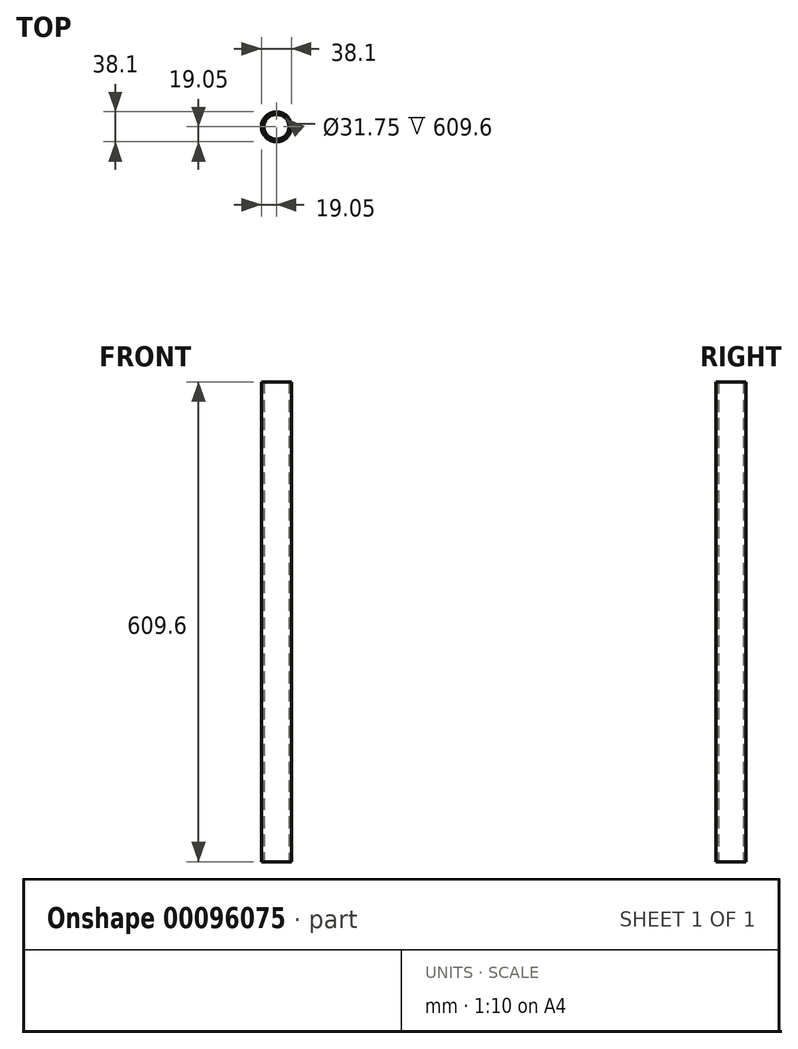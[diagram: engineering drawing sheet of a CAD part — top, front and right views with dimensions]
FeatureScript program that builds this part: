
annotation { "Feature Type Name" : "Feature", "Feature Type Description" : "" }
export const myFeature = defineFeature(function(context is Context, id is Id, definition is map)
    precondition{}
    {
        {
            var Q0;
            Q0=qCreatedBy(makeId("Top.planeOp"),FACE);
            var sketch = newSketch(context, id + "F0", { "sketchPlane" : qUnion([Q0])});
            skCircle(sketch, "E0", {"center": v(0, 0) * mm, "radius": 19.05 * mm});
            skCircle(sketch, "E1", {"center": v(0, 0) * mm, "radius": 15.88 * mm});
            skSolve(sketch);
        }
        {
            var Q0;
            Q0=makeQuery(id+"F0.imprint","IMPRINT",FACE,{"disambiguationData":[TD([[makeQuery(id+"F0.imprint","IMPRINT",EDGE,{"derivedFrom":sQuery(id+"F0.wireOp",EDGE,"E0")}),1.0]])]});
            extrude(context, id + "F1", {"entities" : qUnion([Q0]), "depth" : 609.6 * mm});
        }
        {
            var Q0;
            Q0=qCreatedBy(makeId("Top.planeOp"),FACE);
            cPlane(context, id + "F2", {"entities" : qUnion([Q0]), "cplaneType" : CPlaneType.OFFSET, "offset" : 609.6 * mm, "width" : 152.4 * mm, "height" : 152.4 * mm});
        }
    });
